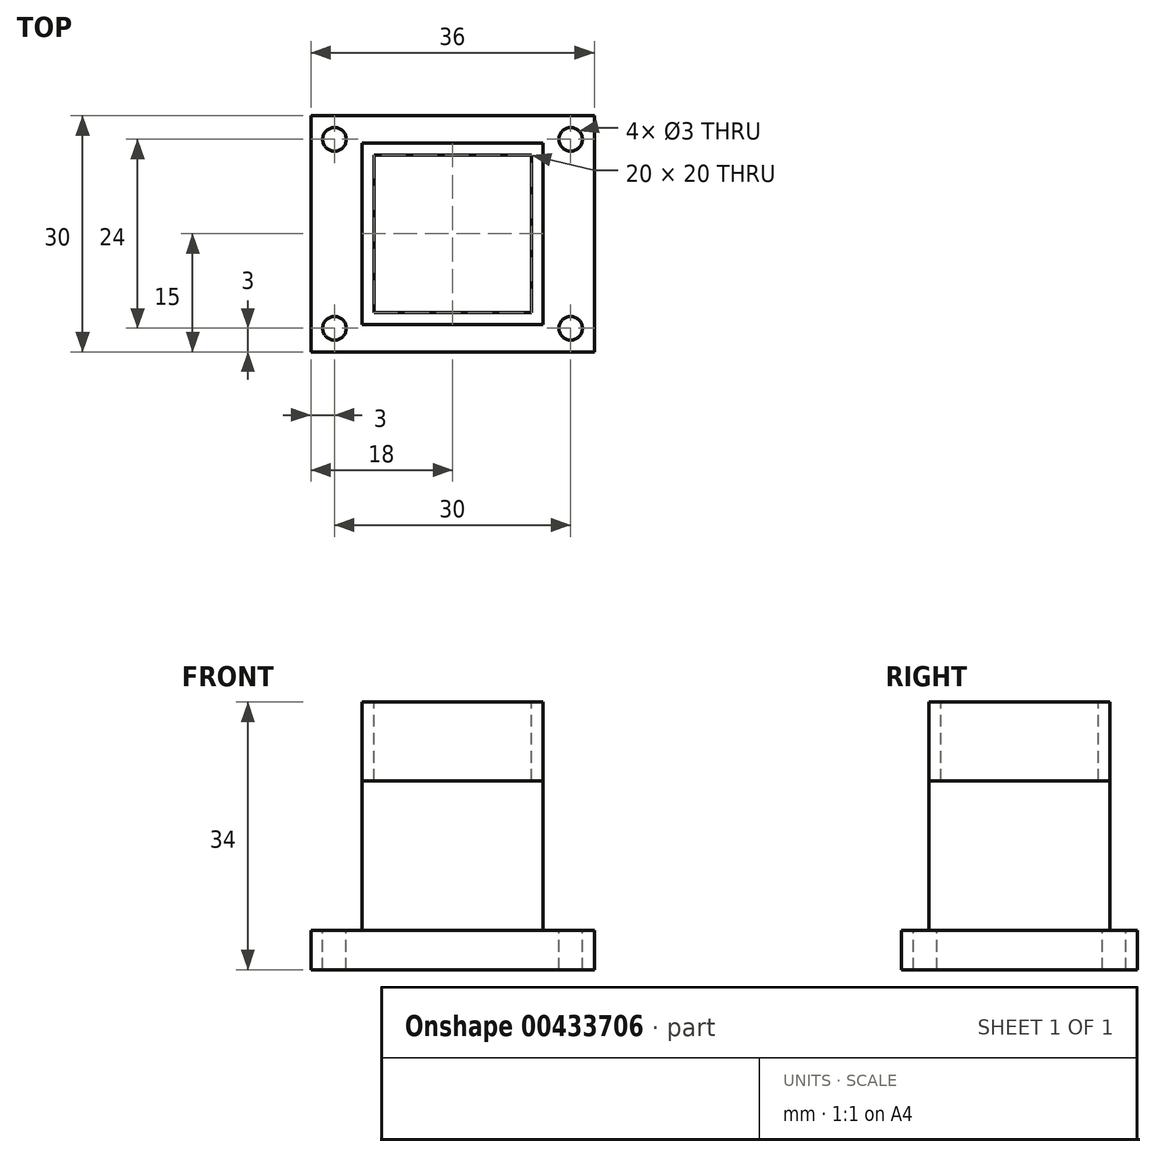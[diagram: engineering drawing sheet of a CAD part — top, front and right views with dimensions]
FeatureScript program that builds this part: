
annotation { "Feature Type Name" : "Feature", "Feature Type Description" : "" }
export const myFeature = defineFeature(function(context is Context, id is Id, definition is map)
    precondition{}
    {
        {
            var Q0;
            Q0=qCreatedBy(makeId("Top.planeOp"),FACE);
            var sketch = newSketch(context, id + "F0", { "sketchPlane" : qUnion([Q0])});
            skLineSegment(sketch, "E0.bottom", {"start": v(18, 15) * mm, "end": v(-18, 15) * mm});
            skLineSegment(sketch, "E0.top", {"start": v(18, -15) * mm, "end": v(-18, -15) * mm});
            skLineSegment(sketch, "E0.left", {"start": v(18, 15) * mm, "end": v(18, -15) * mm});
            skLineSegment(sketch, "E0.right", {"start": v(-18, 15) * mm, "end": v(-18, -15) * mm});
            skPoint(sketch, "E0.middle", {"position": v(0, 0) * mm});
            skSolve(sketch);
        }
        {
            var Q0;
            Q0=makeQuery(id+"F0.imprint","IMPRINT",FACE,{"disambiguationData":[TD([[makeQuery(id+"F0.imprint","IMPRINT",EDGE,{"derivedFrom":sQuery(id+"F0.wireOp",EDGE,"E0.bottom")}),1.0]])]});
            extrude(context, id + "F1", {"entities" : qUnion([Q0]), "depth" : -5 * mm});
        }
        {
            var Q0;
            Q0=qCreatedBy(makeId("Top.planeOp"),FACE);
            var sketch = newSketch(context, id + "F2", { "sketchPlane" : qUnion([Q0])});
            skLineSegment(sketch, "E1.bottom", {"start": v(11.5, -11.5) * mm, "end": v(-11.5, -11.5) * mm});
            skLineSegment(sketch, "E1.top", {"start": v(11.5, 11.5) * mm, "end": v(-11.5, 11.5) * mm});
            skLineSegment(sketch, "E1.left", {"start": v(11.5, -11.5) * mm, "end": v(11.5, 11.5) * mm});
            skLineSegment(sketch, "E1.right", {"start": v(-11.5, -11.5) * mm, "end": v(-11.5, 11.5) * mm});
            skPoint(sketch, "E1.middle", {"position": v(0, 0) * mm});
            skSolve(sketch);
        }
        {
            var Q0;
            Q0 = qSketchRegion(id + "F2", true);
            extrude(context, id + "F3", {"entities" : qUnion([Q0]), "operationType" : NewBodyOperationType.ADD, "depth" : 19 * mm});
        }
        {
            var Q0;
            Q0=qCreatedBy(makeId("Top.planeOp"),FACE);
            var sketch = newSketch(context, id + "F4", { "sketchPlane" : qUnion([Q0])});
            skCircle(sketch, "E2", {"center": v(-15, -12) * mm, "radius": 1.5 * mm});
            skCircle(sketch, "E3", {"center": v(-15, 12) * mm, "radius": 1.5 * mm});
            skCircle(sketch, "E4", {"center": v(15, 12) * mm, "radius": 1.5 * mm});
            skCircle(sketch, "E5", {"center": v(15, -12) * mm, "radius": 1.5 * mm});
            skSolve(sketch);
        }
        {
            var Q0;
            Q0 = qSketchRegion(id + "F4", true);
            extrude(context, id + "F5", {"entities" : qUnion([Q0]), "operationType" : NewBodyOperationType.REMOVE, "oppositeDirection" : true, "depth" : 5 * mm});
        }
        {
            var Q0;
            Q0=makeQuery(id+"F3.opExtrude","CAP_FACE",FACE,{"disambiguationData":[OSD([sQuery(id+"F2.wireOp",EDGE,"E1.bottom"),sQuery(id+"F2.wireOp",EDGE,"E1.top"),sQuery(id+"F2.wireOp",EDGE,"E1.left"),sQuery(id+"F2.wireOp",EDGE,"E1.right")])],"isStart":false});
            var sketch = newSketch(context, id + "F6", { "sketchPlane" : qUnion([Q0])});
            skLineSegment(sketch, "E6.bottom", {"start": v(-11.5, 11.5) * mm, "end": v(11.5, 11.5) * mm});
            skLineSegment(sketch, "E6.top", {"start": v(-11.5, -11.5) * mm, "end": v(11.5, -11.5) * mm});
            skLineSegment(sketch, "E6.left", {"start": v(-11.5, 11.5) * mm, "end": v(-11.5, -11.5) * mm});
            skLineSegment(sketch, "E6.right", {"start": v(11.5, 11.5) * mm, "end": v(11.5, -11.5) * mm});
            skPoint(sketch, "E6.middle", {"position": v(0, 0) * mm});
            skSolve(sketch);
        }
        {
            var Q0;
            Q0 = qSketchRegion(id + "F6", true);
            extrude(context, id + "F7", {"entities" : qUnion([Q0]), "depth" : 10 * mm});
        }
        {
            var Q0;
            Q0=makeQuery(id+"F7.opExtrude","CAP_FACE",FACE,{"disambiguationData":[OSD([sQuery(id+"F6.wireOp",EDGE,"E6.bottom"),sQuery(id+"F6.wireOp",EDGE,"E6.top"),sQuery(id+"F6.wireOp",EDGE,"E6.left"),sQuery(id+"F6.wireOp",EDGE,"E6.right")])],"isStart":false});
            var sketch = newSketch(context, id + "F8", { "sketchPlane" : qUnion([Q0])});
            skLineSegment(sketch, "E7.bottom", {"start": v(-10, 10) * mm, "end": v(10, 10) * mm});
            skLineSegment(sketch, "E7.top", {"start": v(-10, -10) * mm, "end": v(10, -10) * mm});
            skLineSegment(sketch, "E7.left", {"start": v(-10, 10) * mm, "end": v(-10, -10) * mm});
            skLineSegment(sketch, "E7.right", {"start": v(10, 10) * mm, "end": v(10, -10) * mm});
            skPoint(sketch, "E7.middle", {"position": v(0, 0) * mm});
            skSolve(sketch);
        }
        {
            var Q0;
            Q0 = qSketchRegion(id + "F8", true);
            extrude(context, id + "F9", {"entities" : qUnion([Q0]), "operationType" : NewBodyOperationType.REMOVE, "oppositeDirection" : true, "depth" : 10 * mm});
        }
    });
